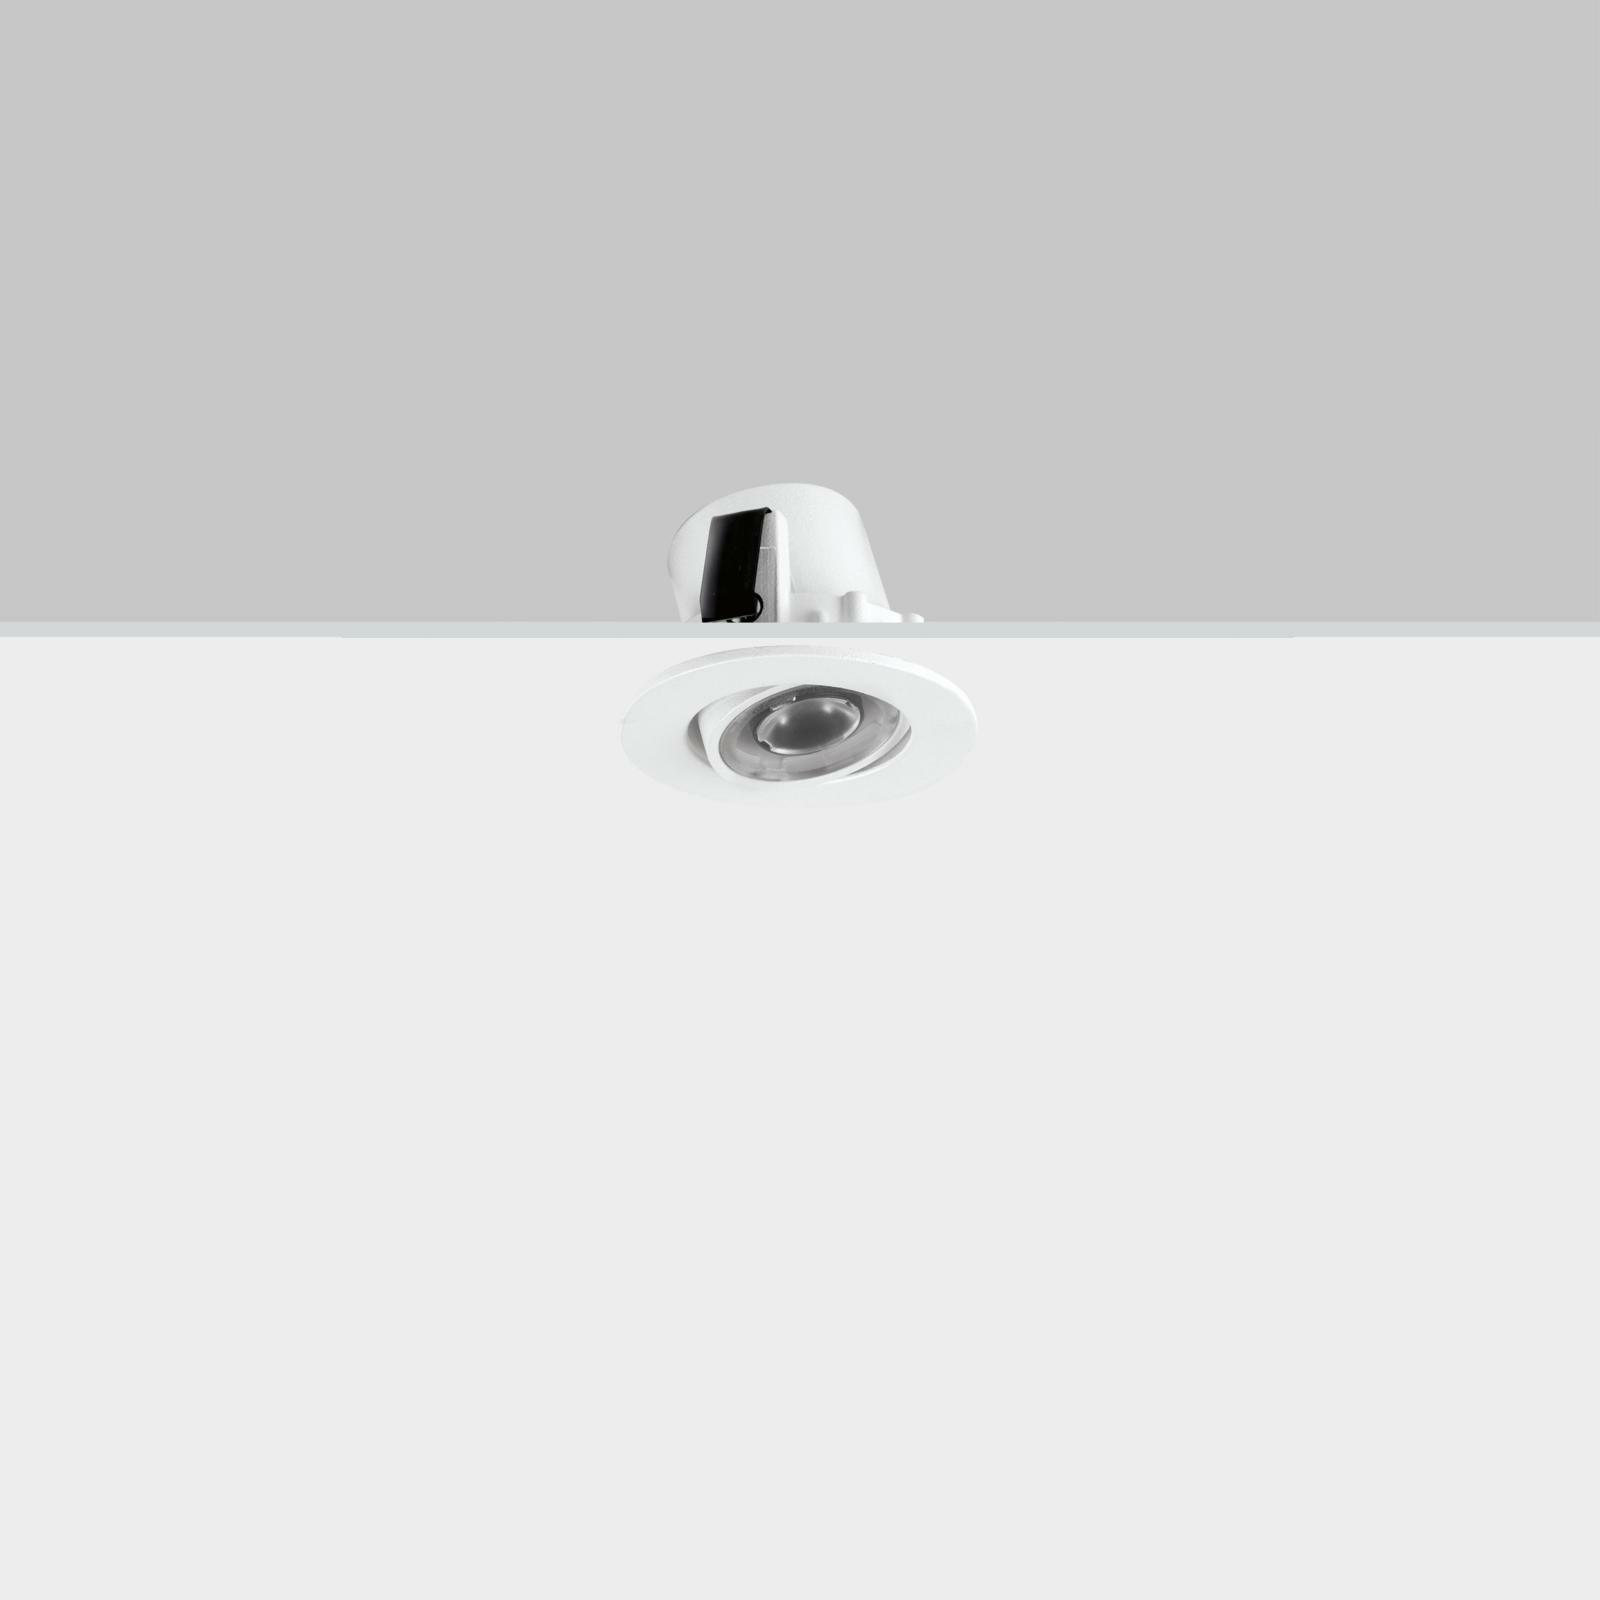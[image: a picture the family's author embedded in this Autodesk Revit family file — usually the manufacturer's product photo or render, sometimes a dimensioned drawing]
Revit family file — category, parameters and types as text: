
# Revit family: RA 4 OSCILLANTE CON LENTE
name_source: partatom
category: Lighting Fixtures
units: mm (PartAtom-declared; Revit-internal decimal feet)

## family parameters
Always vertical = Yes
Cut with Voids When Loaded = No
Host = Ceiling
Light Source = No
OmniClass Number = 23.80.70.11
OmniClass Title = Luminaries for Internal Lighting
Part Type = Normal
Room Calculation Point = No
Round Connector Dimension = Use Diameter
Shared = No

## types (1)
- RA 4 OSCILLANTE CON LENTE
    Body angle = 20.00°
    Body material = White Powder Coated Aluminium
    Description = RA 4 è un incasso oscillante per luce diffusa progettato per fonti luminose LED COB di ultima generazione.
E' caratterizzato da una profondità di incasso estremamente ridotta: l'apparecchio può essere installato facilmente, grazie alle molle laterali, in controsoffitti da 1 a 30 mm.
RA 4 garantisce ottime prestazioni illuminotecniche, è ideale per l'illuminazione in generale di corridoi e zone di passaggio, sia in ambito residenziale sia in spazi pubblici.
LED driver da ordinare separatamente.
    Glass material = Glass
    Larghezza = 50 mm
    Manufacturer = ARIA
    Model = 253-210-21
    Type = RA 4 body : RA 4 OSCILLANTE CON LENTE 200lm 2W 3000K CRI85-WHITE max 20W
    Type Comments = Ceiling recessed light
    Type Image = RA 4 OSCILLANTE CON LENTE_ARIA.jpg
    URL = https://www.aria.lighting

## geometry (parser evidence)
native form markers: Sweep x4
no freeform markers — native parametric forms only
